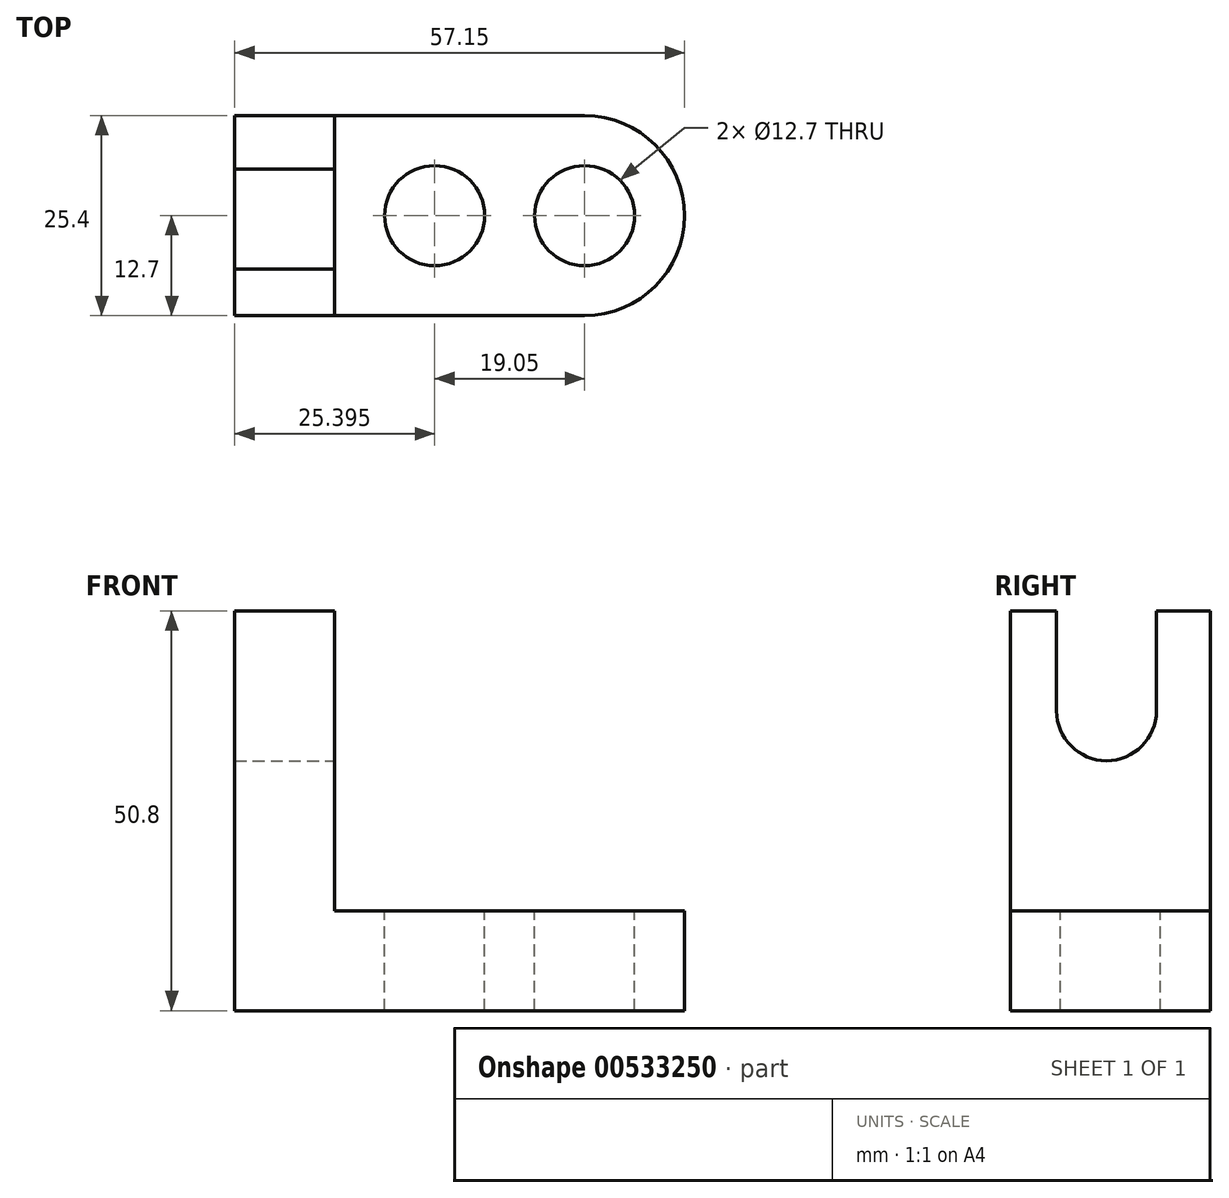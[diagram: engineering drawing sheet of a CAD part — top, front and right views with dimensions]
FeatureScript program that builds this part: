
annotation { "Feature Type Name" : "Feature", "Feature Type Description" : "" }
export const myFeature = defineFeature(function(context is Context, id is Id, definition is map)
    precondition{}
    {
        {
            var Q0;
            Q0=qCreatedBy(makeId("Front.planeOp"),FACE);
            var sketch = newSketch(context, id + "F0", { "sketchPlane" : qUnion([Q0])});
            skLineSegment(sketch, "E0", {"start": v(-59.57, 58.36) * mm, "end": v(-59.57, 7.56) * mm});
            skLineSegment(sketch, "E1", {"start": v(-59.57, 7.56) * mm, "end": v(-2.42, 7.56) * mm});
            skLineSegment(sketch, "E2", {"start": v(-2.42, 7.56) * mm, "end": v(-2.42, 20.26) * mm});
            skLineSegment(sketch, "E3", {"start": v(-2.42, 20.26) * mm, "end": v(-46.87, 20.26) * mm});
            skLineSegment(sketch, "E4", {"start": v(-46.87, 20.26) * mm, "end": v(-46.87, 58.36) * mm});
            skLineSegment(sketch, "E5", {"start": v(-46.87, 58.36) * mm, "end": v(-59.57, 58.36) * mm});
            skSolve(sketch);
        }
        {
            var Q0;
            Q0=makeQuery(id+"F0.imprint","IMPRINT",FACE,{"disambiguationData":[TD([[makeQuery(id+"F0.imprint","IMPRINT",EDGE,{"derivedFrom":sQuery(id+"F0.wireOp",EDGE,"E0")}),1.0]])]});
            extrude(context, id + "F1", {"entities" : qUnion([Q0]), "depth" : 25.4 * mm, "offsetDistance" : 25.4 * mm});
        }
        {
            var Q0;
            Q0=makeQuery(id+"F1.opExtrude","SWEPT_FACE",FACE,{"disambiguationData":[OSD([sQuery(id+"F0.wireOp",EDGE,"E3")])]});
            var sketch = newSketch(context, id + "F2", { "sketchPlane" : qUnion([Q0])});
            skCircle(sketch, "E6", {"center": v(-15.12, -12.7) * mm, "radius": 6.35 * mm});
            skCircle(sketch, "E7", {"center": v(-34.17, -12.7) * mm, "radius": 6.35 * mm});
            skArc(sketch, "E8", {"start": v(-15.12, -25.4) * mm, "mid": v(-2.42, -12.7) * mm, "end": v(-15.12, 0) * mm});
            skSolve(sketch);
        }
        {
            var Q0;
            Q0=makeQuery(id+"F2.imprint","IMPRINT",FACE,{"disambiguationData":[TD([[makeQuery(id+"F2.imprint","IMPRINT",EDGE,{"derivedFrom":sQuery(id+"F2.wireOp",EDGE,"E7")}),1.0]])]});
            var Q1;
            Q1=makeQuery(id+"F2.imprint","IMPRINT",FACE,{"disambiguationData":[TD([[makeQuery(id+"F2.imprint","IMPRINT",EDGE,{"derivedFrom":sQuery(id+"F2.wireOp",EDGE,"E6")}),1.0]])]});
            var Q2;
            {var subQ0=sQuery(id+"F2.wireOp",EDGE,"E8");var subQ1=sQuery(id+"F0.wireOp",EDGE,"E3");var subQ2=makeQuery(id+"F1.opExtrude","CAP_EDGE",EDGE,{"disambiguationData":[OSD([subQ1])],"isStart":true});var subQ3=makeQuery(id+"F2.imprint","INTERSECT",VERTEX,{"derivedFrom":[subQ2,subQ0]});Q2=makeQuery(id+"F2.imprint","IMPRINT",FACE,{"disambiguationData":[TD([[makeQuery(id+"F2.imprint","IMPRINT",EDGE,{"disambiguationData":[TD([[subQ3,1.0]])],"derivedFrom":subQ0}),-1.0]])]});}
            var Q3;
            {var subQ0=sQuery(id+"F2.wireOp",EDGE,"E8");var subQ1=sQuery(id+"F0.wireOp",EDGE,"E3");var subQ2=makeQuery(id+"F1.opExtrude","CAP_EDGE",EDGE,{"disambiguationData":[OSD([subQ1])],"isStart":false});var subQ3=makeQuery(id+"F2.imprint","INTERSECT",VERTEX,{"derivedFrom":[subQ2,subQ0]});Q3=makeQuery(id+"F2.imprint","IMPRINT",FACE,{"disambiguationData":[TD([[makeQuery(id+"F2.imprint","IMPRINT",EDGE,{"disambiguationData":[TD([[subQ3,-1.0]])],"derivedFrom":subQ0}),-1.0]])]});}
            extrude(context, id + "F3", {"entities" : qUnion([Q0, Q1, Q2, Q3]), "operationType" : NewBodyOperationType.REMOVE, "oppositeDirection" : true, "depth" : 25.4 * mm, "offsetDistance" : 25.4 * mm});
        }
        {
            var Q0;
            Q0=makeQuery(id+"F1.opExtrude","SWEPT_FACE",FACE,{"disambiguationData":[OSD([sQuery(id+"F0.wireOp",EDGE,"E4")])]});
            var sketch = newSketch(context, id + "F4", { "sketchPlane" : qUnion([Q0])});
            skCircle(sketch, "E9", {"center": v(-13.17, 45.66) * mm, "radius": 6.35 * mm});
            skLineSegment(sketch, "E10", {"start": v(-6.82, 45.66) * mm, "end": v(-6.82, 58.36) * mm});
            skLineSegment(sketch, "E11", {"start": v(-19.52, 45.66) * mm, "end": v(-19.52, 58.36) * mm});
            skSolve(sketch);
        }
        {
            var Q0;
            {var subQ2=sQuery(id+"F4.wireOp",EDGE,"E10");Q0=makeQuery(id+"F4.imprint","IMPRINT",FACE,{"disambiguationData":[TD([[makeQuery(id+"F4.imprint","IMPRINT",EDGE,{"derivedFrom":subQ2}),-1.0]])]});}
            var sketch = newSketch(context, id + "F5", { "sketchPlane" : qUnion([Q0])});
            skSolve(sketch);
        }
        {
            var Q0;
            {var subQ0=sQuery(id+"F4.wireOp",EDGE,"E9");var subQ1=makeQuery(id+"F4.imprint","INTERSECT",VERTEX,{"derivedFrom":[subQ0,sQuery(id+"F4.wireOp",EDGE,"E10")]});Q0=makeQuery(id+"F4.imprint","IMPRINT",FACE,{"disambiguationData":[TD([[makeQuery(id+"F4.imprint","IMPRINT",EDGE,{"disambiguationData":[TD([[subQ1,-1.0]])],"derivedFrom":subQ0}),1.0]])]});}
            var Q1;
            {var subQ0=sQuery(id+"F4.wireOp",EDGE,"E10");Q1=makeQuery(id+"F4.imprint","IMPRINT",FACE,{"disambiguationData":[TD([[makeQuery(id+"F4.imprint","IMPRINT",EDGE,{"derivedFrom":subQ0}),1.0]])]});}
            extrude(context, id + "F6", {"entities" : qUnion([Q0, Q1]), "operationType" : NewBodyOperationType.REMOVE, "oppositeDirection" : true, "depth" : 25.4 * mm, "offsetDistance" : 25.4 * mm});
        }
    });
